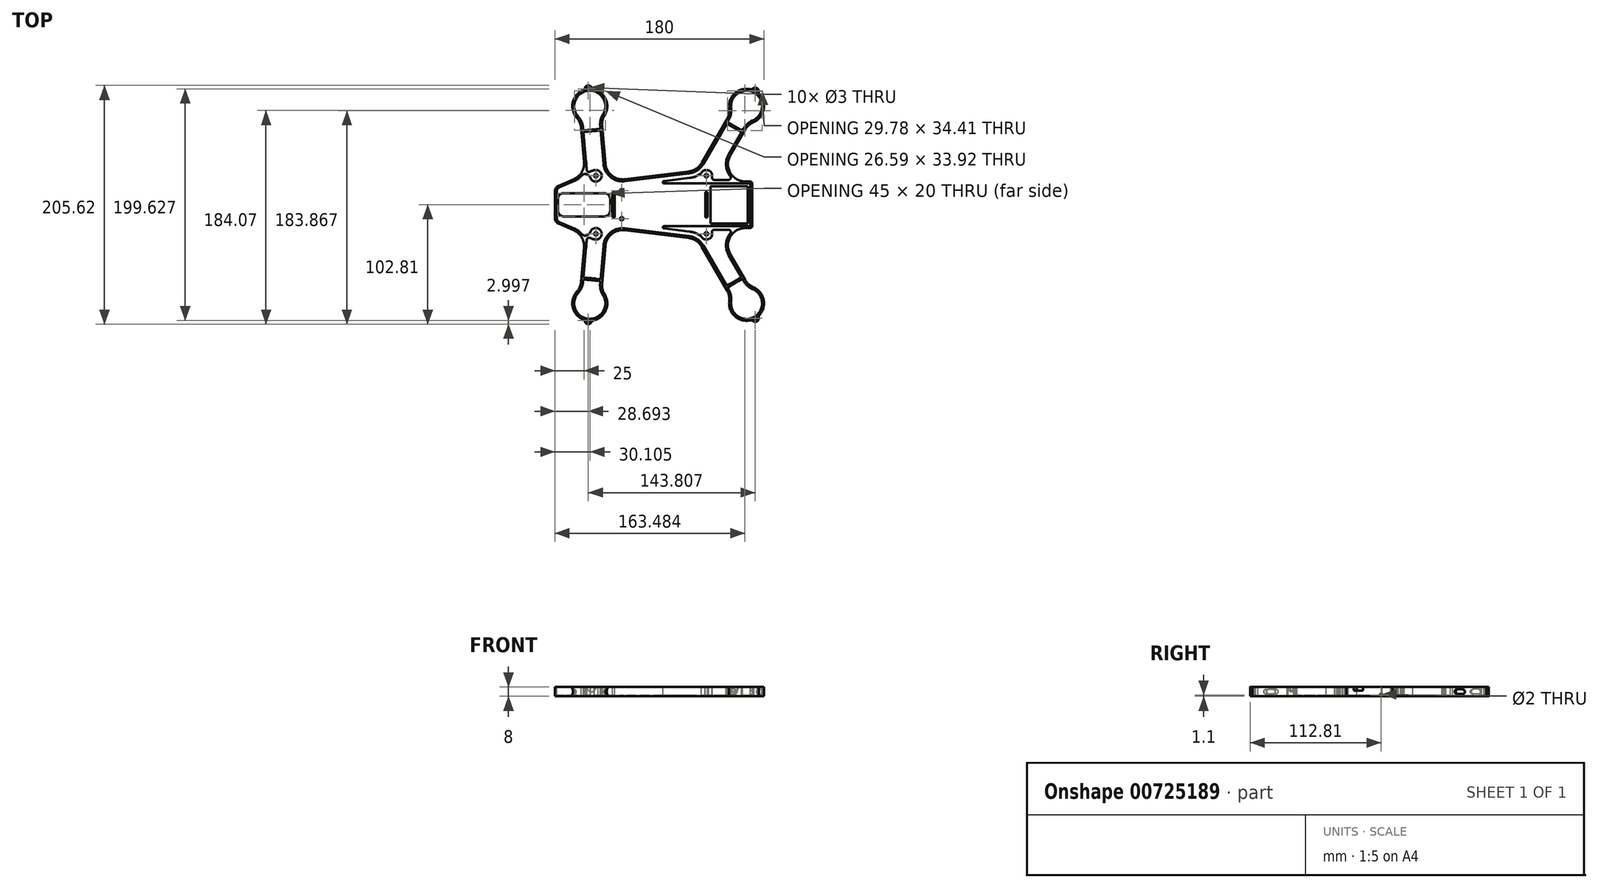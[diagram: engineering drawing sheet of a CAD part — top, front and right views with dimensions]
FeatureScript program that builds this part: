
annotation { "Feature Type Name" : "Feature", "Feature Type Description" : "" }
export const myFeature = defineFeature(function(context is Context, id is Id, definition is map)
    precondition{}
    {
        {
            var Q0;
            Q0=qCreatedBy(makeId("Top.planeOp"),FACE);
            var sketch = newSketch(context, id + "F0", { "sketchPlane" : qUnion([Q0])});
            skLineSegment(sketch, "E0", {"start": v(-85, 0) * mm, "end": v(85, 0) * mm, "construction": true});
            skLineSegment(sketch, "E1", {"start": v(-47.57, 0) * mm, "end": v(-55, -84.87) * mm, "construction": true});
            skLineSegment(sketch, "E2", {"start": v(31, 0) * mm, "end": v(80, -84.87) * mm, "construction": true});
            skArc(sketch, "E3", {"start": v(-66.17, -74.86) * mm, "mid": v(-69.65, -88.1) * mm, "end": v(-60.9, -98.66) * mm});
            skArc(sketch, "E4", {"start": v(65.1, -83.08) * mm, "mid": v(69.86, -95.92) * mm, "end": v(83.07, -99.55) * mm});
            skLineSegment(sketch, "E5", {"start": v(-85, 0) * mm, "end": v(-85, -11.72) * mm});
            skLineSegment(sketch, "E6", {"start": v(-59.85, -37.08) * mm, "end": v(-62.4, -66.15) * mm});
            skLineSegment(sketch, "E7", {"start": v(-44.47, -67.72) * mm, "end": v(-41.64, -35.47) * mm});
            skLineSegment(sketch, "E8", {"start": v(-24.87, -21.9) * mm, "end": v(30.26, -28.66) * mm});
            skLineSegment(sketch, "E9", {"start": v(41.42, -36.05) * mm, "end": v(63.2, -73.78) * mm});
            skLineSegment(sketch, "E10", {"start": v(78.8, -64.78) * mm, "end": v(65.93, -42.5) * mm});
            skLineSegment(sketch, "E11", {"start": v(78.92, -20) * mm, "end": v(83, -20) * mm});
            skLineSegment(sketch, "E12", {"start": v(85, -18) * mm, "end": v(85, 0) * mm});
            skPoint(sketch, "E13.visualSharp", {"position": v(-40.3, -20) * mm});
            skArc(sketch, "E13.filletArc", {"start": v(-24.87, -21.9) * mm, "mid": v(-36.14, -25.12) * mm, "end": v(-41.64, -35.47) * mm});
            skPoint(sketch, "E14.visualSharp", {"position": v(52.94, -20) * mm});
            skPoint(sketch, "E15.visualSharp", {"position": v(37.68, -29.57) * mm});
            skArc(sketch, "E15.filletArc", {"start": v(41.42, -36.05) * mm, "mid": v(36.71, -31.04) * mm, "end": v(30.26, -28.66) * mm});
            skPoint(sketch, "E16.visualSharp", {"position": v(85, -20) * mm});
            skArc(sketch, "E16.filletArc", {"start": v(83, -20) * mm, "mid": v(84.41, -19.41) * mm, "end": v(85, -18) * mm});
            skArc(sketch, "E17.filletArc", {"start": v(78.92, -20) * mm, "mid": v(65.93, -27.5) * mm, "end": v(65.93, -42.5) * mm});
            skPoint(sketch, "E18.visualSharp", {"position": v(-62.92, -72.13) * mm});
            skArc(sketch, "E18.filletArc", {"start": v(-66.17, -74.86) * mm, "mid": v(-63.58, -70.81) * mm, "end": v(-62.4, -66.15) * mm});
            skPoint(sketch, "E19.visualSharp", {"position": v(-44.99, -73.7) * mm});
            skArc(sketch, "E19.filletArc", {"start": v(-44.47, -67.72) * mm, "mid": v(-44.11, -72.52) * mm, "end": v(-42.26, -76.95) * mm});
            skArc(sketch, "E20.filletArc", {"start": v(65.1, -83.08) * mm, "mid": v(64.91, -78.27) * mm, "end": v(63.2, -73.78) * mm});
            skPoint(sketch, "E21.visualSharp", {"position": v(81.8, -69.98) * mm});
            skArc(sketch, "E21.filletArc", {"start": v(78.8, -64.78) * mm, "mid": v(81.83, -68.5) * mm, "end": v(85.9, -71.08) * mm});
            skLineSegment(sketch, "E22", {"start": v(-81.99, -16.3) * mm, "end": v(-68.83, -22) * mm});
            skPoint(sketch, "E23.visualSharp", {"position": v(-85, -15) * mm});
            skArc(sketch, "E23.filletArc", {"start": v(-85, -11.72) * mm, "mid": v(-84.18, -14.46) * mm, "end": v(-81.99, -16.3) * mm});
            skPoint(sketch, "E24.visualSharp", {"position": v(-58.91, -26.3) * mm});
            skArc(sketch, "E25.filletArc", {"start": v(-59.85, -37.08) * mm, "mid": v(-61.9, -28.1) * mm, "end": v(-68.83, -22) * mm});
            skLineSegment(sketch, "E26", {"start": v(78.92, -20) * mm, "end": v(-122.08, -20) * mm, "construction": true});
            skLineSegment(sketch, "E27", {"start": v(-55, -84.87) * mm, "end": v(-57.29, -111.02) * mm, "construction": true});
            skLineSegment(sketch, "E28", {"start": v(80, -84.87) * mm, "end": v(94.45, -109.9) * mm, "construction": true});
            skArc(sketch, "E29.trimOffspring", {"start": v(-51.58, -99.47) * mm, "mid": v(-41.14, -90.6) * mm, "end": v(-42.26, -76.95) * mm});
            skCircle(sketch, "E30", {"center": v(87.5, -97.86) * mm, "radius": 1.5 * mm});
            skArc(sketch, "E31", {"start": v(85.6, -100.18) * mm, "mid": v(89, -100.46) * mm, "end": v(90.46, -97.37) * mm});
            skArc(sketch, "E32.trimOffspring", {"start": v(91.18, -94.87) * mm, "mid": v(94.64, -81.62) * mm, "end": v(85.9, -71.08) * mm});
            skPoint(sketch, "E33.visualSharp", {"position": v(89.94, -96.1) * mm});
            skArc(sketch, "E33.filletArc", {"start": v(91.18, -94.87) * mm, "mid": v(90.54, -96.04) * mm, "end": v(90.46, -97.37) * mm});
            skPoint(sketch, "E34.visualSharp", {"position": v(84.76, -99.1) * mm});
            skArc(sketch, "E35.filletArc", {"start": v(85.6, -100.18) * mm, "mid": v(84.4, -99.58) * mm, "end": v(83.07, -99.55) * mm});
            skCircle(sketch, "E36", {"center": v(-49.76, -25) * mm, "radius": 1.5 * mm});
            skCircle(sketch, "E37", {"center": v(45.43, -25) * mm, "radius": 1.5 * mm});
            skCircle(sketch, "E38", {"center": v(-56.3, -99.81) * mm, "radius": 1.5 * mm});
            skArc(sketch, "E39", {"start": v(-59.2, -100.61) * mm, "mid": v(-56.57, -102.8) * mm, "end": v(-53.6, -101.1) * mm});
            skPoint(sketch, "E40.visualSharp", {"position": v(-53.3, -99.77) * mm});
            skArc(sketch, "E40.filletArc", {"start": v(-51.58, -99.47) * mm, "mid": v(-52.77, -100.06) * mm, "end": v(-53.6, -101.1) * mm});
            skPoint(sketch, "E41.visualSharp", {"position": v(-59.25, -99.25) * mm});
            skArc(sketch, "E41.filletArc", {"start": v(-59.2, -100.61) * mm, "mid": v(-59.83, -99.44) * mm, "end": v(-60.9, -98.66) * mm});
            skLineSegment(sketch, "E42", {"start": v(-55, -84.87) * mm, "end": v(80, -84.87) * mm, "construction": true});
            skLineSegment(sketch, "E43", {"start": v(85, -15) * mm, "end": v(-122.38, -15) * mm, "construction": true});
            skLineSegment(sketch, "E44.2", {"start": v(78.92, -18.4) * mm, "end": v(80, -18.4) * mm});
            skLineSegment(sketch, "E44.4", {"start": v(77.4, -65.58) * mm, "end": v(76.4, -63.85) * mm});
            skArc(sketch, "E44.5", {"start": v(-51.94, -97.92) * mm, "mid": v(-42.62, -90) * mm, "end": v(-43.62, -77.8) * mm});
            skArc(sketch, "E44.8", {"start": v(-64.98, -75.93) * mm, "mid": v(-66.53, -91.7) * mm, "end": v(-51.94, -97.92) * mm});
            skArc(sketch, "E44.9", {"start": v(-64.98, -75.93) * mm, "mid": v(-62.1, -71.45) * mm, "end": v(-60.8, -66.3) * mm});
            skArc(sketch, "E44.15", {"start": v(-46.06, -67.58) * mm, "mid": v(-45.67, -72.89) * mm, "end": v(-43.62, -77.8) * mm});
            skLineSegment(sketch, "E44.16", {"start": v(-46.06, -67.58) * mm, "end": v(-45.89, -65.6) * mm});
            skLineSegment(sketch, "E44.19", {"start": v(30.45, -27.07) * mm, "end": v(30.45, -27.07) * mm});
            skArc(sketch, "E44.21", {"start": v(66.7, -83.27) * mm, "mid": v(66.48, -77.95) * mm, "end": v(64.6, -72.98) * mm});
            skArc(sketch, "E44.22", {"start": v(66.7, -83.27) * mm, "mid": v(74.48, -97.08) * mm, "end": v(89.99, -93.8) * mm});
            skArc(sketch, "E44.25", {"start": v(89.99, -93.8) * mm, "mid": v(93.08, -81.96) * mm, "end": v(85.26, -72.55) * mm});
            skArc(sketch, "E44.26", {"start": v(77.4, -65.58) * mm, "mid": v(80.77, -69.7) * mm, "end": v(85.26, -72.55) * mm});
            skPoint(sketch, "E45.visualSharp", {"position": v(-2, -22.69) * mm});
            skPoint(sketch, "E46.visualSharp", {"position": v(2, -23.18) * mm});
            skLineSegment(sketch, "E47.trimOffspring", {"start": v(-43.24, -35.33) * mm, "end": v(-43.24, -35.33) * mm});
            skLineSegment(sketch, "E48.MirrorCS", {"start": v(78.92, 20) * mm, "end": v(83, 20) * mm});
            skArc(sketch, "E49.MirrorCS", {"start": v(91.18, 94.87) * mm, "mid": v(90.54, 96.04) * mm, "end": v(90.46, 97.37) * mm});
            skLineSegment(sketch, "E50.MirrorCS", {"start": v(78.92, 18.4) * mm, "end": v(80, 18.4) * mm});
            skArc(sketch, "E51.MirrorCS", {"start": v(85.6, 100.18) * mm, "mid": v(84.4, 99.58) * mm, "end": v(83.07, 99.55) * mm});
            skPoint(sketch, "E52.MirrorP", {"position": v(-58.91, 26.3) * mm});
            skPoint(sketch, "E53.MirrorP", {"position": v(52.94, 20) * mm});
            skCircle(sketch, "E54.MirrorC", {"center": v(-56.3, 99.81) * mm, "radius": 1.5 * mm});
            skPoint(sketch, "E55.MirrorP", {"position": v(84.76, 99.1) * mm});
            skArc(sketch, "E56.MirrorCS", {"start": v(-64.98, 75.93) * mm, "mid": v(-62.1, 71.45) * mm, "end": v(-60.8, 66.3) * mm});
            skLineSegment(sketch, "E57.MirrorCS", {"start": v(-44.47, 67.72) * mm, "end": v(-41.64, 35.47) * mm});
            skLineSegment(sketch, "E58.MirrorCS", {"start": v(80, 84.87) * mm, "end": v(94.45, 109.9) * mm, "construction": true});
            skPoint(sketch, "E59.MirrorP", {"position": v(-62.92, 72.13) * mm});
            skPoint(sketch, "E60.MirrorP", {"position": v(-59.25, 99.25) * mm});
            skArc(sketch, "E61.MirrorCS", {"start": v(-24.87, 21.9) * mm, "mid": v(-36.14, 25.12) * mm, "end": v(-41.64, 35.47) * mm});
            skArc(sketch, "E62.MirrorCS", {"start": v(-85, 11.72) * mm, "mid": v(-84.18, 14.46) * mm, "end": v(-81.99, 16.3) * mm});
            skPoint(sketch, "E63.MirrorP", {"position": v(37.68, 29.57) * mm});
            skArc(sketch, "E64.MirrorCS", {"start": v(89.99, 93.8) * mm, "mid": v(93.08, 81.96) * mm, "end": v(85.26, 72.55) * mm});
            skLineSegment(sketch, "E65.MirrorCS", {"start": v(77.4, 65.58) * mm, "end": v(76.4, 63.85) * mm});
            skLineSegment(sketch, "E66.MirrorCS", {"start": v(-24.87, 21.9) * mm, "end": v(30.26, 28.66) * mm});
            skPoint(sketch, "E67.MirrorP", {"position": v(89.94, 96.1) * mm});
            skLineSegment(sketch, "E68.MirrorCS", {"start": v(30.45, 27.07) * mm, "end": v(30.45, 27.07) * mm});
            skCircle(sketch, "E69.MirrorC", {"center": v(45.43, 25) * mm, "radius": 1.5 * mm});
            skCircle(sketch, "E70.MirrorC", {"center": v(87.5, 97.86) * mm, "radius": 1.5 * mm});
            skLineSegment(sketch, "E71.MirrorCS", {"start": v(-55, 84.87) * mm, "end": v(80, 84.87) * mm, "construction": true});
            skArc(sketch, "E72.MirrorCS", {"start": v(-59.2, 100.61) * mm, "mid": v(-56.57, 102.8) * mm, "end": v(-53.6, 101.1) * mm});
            skLineSegment(sketch, "E73.MirrorCS", {"start": v(31, 0) * mm, "end": v(80, 84.87) * mm, "construction": true});
            skArc(sketch, "E74.MirrorCS", {"start": v(-66.17, 74.86) * mm, "mid": v(-63.58, 70.81) * mm, "end": v(-62.4, 66.15) * mm});
            skLineSegment(sketch, "E75.MirrorCS", {"start": v(85, 15) * mm, "end": v(-122.38, 15) * mm, "construction": true});
            skLineSegment(sketch, "E76.MirrorCS", {"start": v(-43.24, 35.33) * mm, "end": v(-43.24, 35.33) * mm});
            skArc(sketch, "E77.MirrorCS", {"start": v(77.4, 65.58) * mm, "mid": v(80.77, 69.7) * mm, "end": v(85.26, 72.55) * mm});
            skPoint(sketch, "E78.MirrorP", {"position": v(-2, 22.69) * mm});
            skArc(sketch, "E79.MirrorCS", {"start": v(-66.17, 74.86) * mm, "mid": v(-69.65, 88.1) * mm, "end": v(-60.9, 98.66) * mm});
            skPoint(sketch, "E80.MirrorP", {"position": v(81.8, 69.98) * mm});
            skLineSegment(sketch, "E81.MirrorCS", {"start": v(-46.06, 67.58) * mm, "end": v(-45.89, 65.6) * mm});
            skArc(sketch, "E82.MirrorCS", {"start": v(78.8, 64.78) * mm, "mid": v(81.83, 68.5) * mm, "end": v(85.9, 71.08) * mm});
            skArc(sketch, "E83.MirrorCS", {"start": v(-59.85, 37.08) * mm, "mid": v(-61.9, 28.1) * mm, "end": v(-68.83, 22) * mm});
            skLineSegment(sketch, "E84.MirrorCS", {"start": v(78.92, 20) * mm, "end": v(-122.08, 20) * mm, "construction": true});
            skArc(sketch, "E85.MirrorCS", {"start": v(66.7, 83.27) * mm, "mid": v(74.48, 97.08) * mm, "end": v(89.99, 93.8) * mm});
            skArc(sketch, "E86.MirrorCS", {"start": v(65.1, 83.08) * mm, "mid": v(69.86, 95.92) * mm, "end": v(83.07, 99.55) * mm});
            skArc(sketch, "E87.MirrorCS", {"start": v(-51.58, 99.47) * mm, "mid": v(-41.14, 90.6) * mm, "end": v(-42.26, 76.95) * mm});
            skPoint(sketch, "E88.MirrorP", {"position": v(-53.3, 99.77) * mm});
            skArc(sketch, "E89.MirrorCS", {"start": v(91.18, 94.87) * mm, "mid": v(94.64, 81.62) * mm, "end": v(85.9, 71.08) * mm});
            skArc(sketch, "E90.MirrorCS", {"start": v(41.42, 36.05) * mm, "mid": v(36.71, 31.04) * mm, "end": v(30.26, 28.66) * mm});
            skArc(sketch, "E91.MirrorCS", {"start": v(-64.98, 75.93) * mm, "mid": v(-66.53, 91.7) * mm, "end": v(-51.94, 97.92) * mm});
            skArc(sketch, "E92.MirrorCS", {"start": v(-51.94, 97.92) * mm, "mid": v(-42.62, 90) * mm, "end": v(-43.62, 77.8) * mm});
            skArc(sketch, "E93.MirrorCS", {"start": v(-44.47, 67.72) * mm, "mid": v(-44.11, 72.52) * mm, "end": v(-42.26, 76.95) * mm});
            skLineSegment(sketch, "E94.MirrorCS", {"start": v(-47.57, 0) * mm, "end": v(-55, 84.87) * mm, "construction": true});
            skLineSegment(sketch, "E95.MirrorCS", {"start": v(78.8, 64.78) * mm, "end": v(65.93, 42.5) * mm});
            skLineSegment(sketch, "E96.MirrorCS", {"start": v(41.42, 36.05) * mm, "end": v(63.2, 73.78) * mm});
            skArc(sketch, "E97.MirrorCS", {"start": v(85.6, 100.18) * mm, "mid": v(89, 100.46) * mm, "end": v(90.46, 97.37) * mm});
            skArc(sketch, "E98.MirrorCS", {"start": v(-46.06, 67.58) * mm, "mid": v(-45.67, 72.89) * mm, "end": v(-43.62, 77.8) * mm});
            skLineSegment(sketch, "E99.MirrorCS", {"start": v(-85, 0) * mm, "end": v(-85, 11.72) * mm});
            skArc(sketch, "E100.MirrorCS", {"start": v(65.1, 83.08) * mm, "mid": v(64.91, 78.27) * mm, "end": v(63.2, 73.78) * mm});
            skArc(sketch, "E101.MirrorCS", {"start": v(78.92, 20) * mm, "mid": v(65.93, 27.5) * mm, "end": v(65.93, 42.5) * mm});
            skArc(sketch, "E102.MirrorCS", {"start": v(66.7, 83.27) * mm, "mid": v(66.48, 77.95) * mm, "end": v(64.6, 72.98) * mm});
            skLineSegment(sketch, "E103.MirrorCS", {"start": v(-55, 84.87) * mm, "end": v(-57.29, 111.02) * mm, "construction": true});
            skPoint(sketch, "E104.MirrorP", {"position": v(-44.99, 73.7) * mm});
            skCircle(sketch, "E105.MirrorC", {"center": v(-49.76, 25) * mm, "radius": 1.5 * mm});
            skPoint(sketch, "E106.MirrorP", {"position": v(-85, 15) * mm});
            skPoint(sketch, "E107.MirrorP", {"position": v(85, 20) * mm});
            skLineSegment(sketch, "E108.MirrorCS", {"start": v(85, 18) * mm, "end": v(85, 0) * mm});
            skArc(sketch, "E109.MirrorCS", {"start": v(83, 20) * mm, "mid": v(84.41, 19.41) * mm, "end": v(85, 18) * mm});
            skPoint(sketch, "E110.MirrorP", {"position": v(-40.3, 20) * mm});
            skLineSegment(sketch, "E111.MirrorCS", {"start": v(-81.99, 16.3) * mm, "end": v(-68.83, 22) * mm});
            skLineSegment(sketch, "E112.MirrorCS", {"start": v(-59.85, 37.08) * mm, "end": v(-62.4, 66.15) * mm});
            skPoint(sketch, "E113.MirrorP", {"position": v(2, 23.18) * mm});
            skArc(sketch, "E114.filletArc", {"start": v(-60.9, 98.66) * mm, "mid": v(-59.83, 99.44) * mm, "end": v(-59.2, 100.61) * mm});
            skArc(sketch, "E115.filletArc", {"start": v(-53.6, 101.1) * mm, "mid": v(-52.77, 100.06) * mm, "end": v(-51.58, 99.47) * mm});
            skLineSegment(sketch, "E116", {"start": v(-60.63, -64.3) * mm, "end": v(-45.89, -65.6) * mm});
            skLineSegment(sketch, "E117.trimOffspring", {"start": v(-60.63, -64.3) * mm, "end": v(-60.8, -66.3) * mm});
            skLineSegment(sketch, "E118", {"start": v(63.6, -71.25) * mm, "end": v(76.4, -63.85) * mm});
            skLineSegment(sketch, "E119.trimOffspring", {"start": v(63.6, -71.25) * mm, "end": v(64.6, -72.98) * mm});
            skLineSegment(sketch, "E120.MirrorCS", {"start": v(-60.63, 64.3) * mm, "end": v(-45.89, 65.6) * mm});
            skLineSegment(sketch, "E121.MirrorCS", {"start": v(63.6, 71.25) * mm, "end": v(76.4, 63.85) * mm});
            skLineSegment(sketch, "E122.trimOffspring", {"start": v(63.6, 71.25) * mm, "end": v(64.6, 72.98) * mm});
            skLineSegment(sketch, "E123.trimOffspring", {"start": v(-60.63, 64.3) * mm, "end": v(-60.8, 66.3) * mm});
            skCircle(sketch, "E124", {"center": v(0, 0) * mm, "radius": 134.27 * mm, "construction": true});
            skLineSegment(sketch, "E125.bottom", {"start": v(-42.5, -10) * mm, "end": v(-77.5, -10) * mm});
            skLineSegment(sketch, "E125.top", {"start": v(-42.5, 10) * mm, "end": v(-77.5, 10) * mm});
            skLineSegment(sketch, "E125.left", {"start": v(-37.5, -5) * mm, "end": v(-37.5, 5) * mm});
            skLineSegment(sketch, "E125.right", {"start": v(-82.5, -5) * mm, "end": v(-82.5, 5) * mm});
            skArc(sketch, "E126.filletArc", {"start": v(-37.5, 5) * mm, "mid": v(-38.96, 8.54) * mm, "end": v(-42.5, 10) * mm});
            skArc(sketch, "E127.filletArc", {"start": v(-82.5, -5) * mm, "mid": v(-81.04, -8.54) * mm, "end": v(-77.5, -10) * mm});
            skArc(sketch, "E128.filletArc", {"start": v(-77.5, 10) * mm, "mid": v(-81.04, 8.54) * mm, "end": v(-82.5, 5) * mm});
            skArc(sketch, "E129.filletArc", {"start": v(-42.5, -10) * mm, "mid": v(-38.96, -8.54) * mm, "end": v(-37.5, -5) * mm});
            skCircle(sketch, "E130", {"center": v(-27.5, -12) * mm, "radius": 1.5 * mm});
            skCircle(sketch, "E131.MirrorC", {"center": v(-27.5, 12) * mm, "radius": 1.5 * mm});
            skSolve(sketch);
        }
        {
            var Q0;
            Q0=makeQuery(id+"F0.imprint","IMPRINT",FACE,{"disambiguationData":[TD([[makeQuery(id+"F0.imprint","IMPRINT",EDGE,{"derivedFrom":sQuery(id+"F0.wireOp",EDGE,"E3")}),1.0]])]});
            extrude(context, id + "F1", {"entities" : qUnion([Q0]), "depth" : 8 * mm});
        }
        {
            var Q0;
            Q0=makeQuery(id+"F1.opExtrude","CAP_FACE",FACE,{"disambiguationData":[OSD([sQuery(id+"F0.wireOp",EDGE,"E3"),sQuery(id+"F0.wireOp",EDGE,"E4"),sQuery(id+"F0.wireOp",EDGE,"E5"),sQuery(id+"F0.wireOp",EDGE,"E6"),sQuery(id+"F0.wireOp",EDGE,"E7"),sQuery(id+"F0.wireOp",EDGE,"E8"),sQuery(id+"F0.wireOp",EDGE,"E9"),sQuery(id+"F0.wireOp",EDGE,"E10"),sQuery(id+"F0.wireOp",EDGE,"E11"),sQuery(id+"F0.wireOp",EDGE,"E12"),sQuery(id+"F0.wireOp",EDGE,"E13.filletArc"),sQuery(id+"F0.wireOp",EDGE,"E15.filletArc"),sQuery(id+"F0.wireOp",EDGE,"E16.filletArc"),sQuery(id+"F0.wireOp",EDGE,"E17.filletArc"),sQuery(id+"F0.wireOp",EDGE,"E18.filletArc"),sQuery(id+"F0.wireOp",EDGE,"E19.filletArc"),sQuery(id+"F0.wireOp",EDGE,"E20.filletArc"),sQuery(id+"F0.wireOp",EDGE,"E21.filletArc"),sQuery(id+"F0.wireOp",EDGE,"E22"),sQuery(id+"F0.wireOp",EDGE,"E23.filletArc"),sQuery(id+"F0.wireOp",EDGE,"E25.filletArc"),sQuery(id+"F0.wireOp",EDGE,"E29.trimOffspring"),sQuery(id+"F0.wireOp",EDGE,"E30"),sQuery(id+"F0.wireOp",EDGE,"E31"),sQuery(id+"F0.wireOp",EDGE,"E32.trimOffspring"),sQuery(id+"F0.wireOp",EDGE,"E33.filletArc"),sQuery(id+"F0.wireOp",EDGE,"E35.filletArc"),sQuery(id+"F0.wireOp",EDGE,"E36"),sQuery(id+"F0.wireOp",EDGE,"E37"),sQuery(id+"F0.wireOp",EDGE,"E38"),sQuery(id+"F0.wireOp",EDGE,"E39"),sQuery(id+"F0.wireOp",EDGE,"E40.filletArc"),sQuery(id+"F0.wireOp",EDGE,"E41.filletArc"),sQuery(id+"F0.wireOp",EDGE,"E44.4"),sQuery(id+"F0.wireOp",EDGE,"E44.5"),sQuery(id+"F0.wireOp",EDGE,"E44.8"),sQuery(id+"F0.wireOp",EDGE,"E44.9"),sQuery(id+"F0.wireOp",EDGE,"E44.10"),sQuery(id+"F0.wireOp",EDGE,"E44.11"),sQuery(id+"F0.wireOp",EDGE,"E44.12"),sQuery(id+"F0.wireOp",EDGE,"E44.13"),sQuery(id+"F0.wireOp",EDGE,"E44.15"),sQuery(id+"F0.wireOp",EDGE,"E44.16"),sQuery(id+"F0.wireOp",EDGE,"E44.20"),sQuery(id+"F0.wireOp",EDGE,"E44.21"),sQuery(id+"F0.wireOp",EDGE,"E44.22"),sQuery(id+"F0.wireOp",EDGE,"E44.25"),sQuery(id+"F0.wireOp",EDGE,"E44.26"),sQuery(id+"F0.wireOp",EDGE,"55a75c94-3981-4925-938c-0703a2540f2a"),sQuery(id+"F0.wireOp",EDGE,"18e9a88f-63d2-484e-94f8-6aafb132c643"),sQuery(id+"F0.wireOp",EDGE,"3e357946-6a65-48ba-9413-4c9084a4b4eb"),sQuery(id+"F0.wireOp",EDGE,"9b53bd53-ce0e-4c03-85f3-8b744b70c49f.trimOffspring"),sQuery(id+"F0.wireOp",EDGE,"E48.MirrorCS"),sQuery(id+"F0.wireOp",EDGE,"E49.MirrorCS"),sQuery(id+"F0.wireOp",EDGE,"E51.MirrorCS"),sQuery(id+"F0.wireOp",EDGE,"E54.MirrorC"),sQuery(id+"F0.wireOp",EDGE,"E56.MirrorCS"),sQuery(id+"F0.wireOp",EDGE,"E57.MirrorCS"),sQuery(id+"F0.wireOp",EDGE,"E61.MirrorCS"),sQuery(id+"F0.wireOp",EDGE,"E62.MirrorCS"),sQuery(id+"F0.wireOp",EDGE,"E64.MirrorCS"),sQuery(id+"F0.wireOp",EDGE,"E65.MirrorCS"),sQuery(id+"F0.wireOp",EDGE,"E66.MirrorCS"),sQuery(id+"F0.wireOp",EDGE,"E69.MirrorC"),sQuery(id+"F0.wireOp",EDGE,"E508.MirrorCS"),sQuery(id+"F0.wireOp",EDGE,"E70.MirrorC"),sQuery(id+"F0.wireOp",EDGE,"7aa77c07-5236-4930-a80c-88c67a00b59931.MirrorCS"),sQuery(id+"F0.wireOp",EDGE,"E72.MirrorCS"),sQuery(id+"F0.wireOp",EDGE,"E74.MirrorCS"),sQuery(id+"F0.wireOp",EDGE,"7aa77c07-5236-4930-a80c-88c67a00b59935.MirrorCS"),sQuery(id+"F0.wireOp",EDGE,"7aa77c07-5236-4930-a80c-88c67a00b59937.MirrorCS"),sQuery(id+"F0.wireOp",EDGE,"E77.MirrorCS"),sQuery(id+"F0.wireOp",EDGE,"E79.MirrorCS"),sQuery(id+"F0.wireOp",EDGE,"E81.MirrorCS"),sQuery(id+"F0.wireOp",EDGE,"E82.MirrorCS"),sQuery(id+"F0.wireOp",EDGE,"E83.MirrorCS"),sQuery(id+"F0.wireOp",EDGE,"E85.MirrorCS"),sQuery(id+"F0.wireOp",EDGE,"E86.MirrorCS"),sQuery(id+"F0.wireOp",EDGE,"E87.MirrorCS"),sQuery(id+"F0.wireOp",EDGE,"E89.MirrorCS"),sQuery(id+"F0.wireOp",EDGE,"E90.MirrorCS"),sQuery(id+"F0.wireOp",EDGE,"E91.MirrorCS"),sQuery(id+"F0.wireOp",EDGE,"E92.MirrorCS"),sQuery(id+"F0.wireOp",EDGE,"E93.MirrorCS"),sQuery(id+"F0.wireOp",EDGE,"E95.MirrorCS"),sQuery(id+"F0.wireOp",EDGE,"E96.MirrorCS"),sQuery(id+"F0.wireOp",EDGE,"E97.MirrorCS"),sQuery(id+"F0.wireOp",EDGE,"E98.MirrorCS"),sQuery(id+"F0.wireOp",EDGE,"E99.MirrorCS"),sQuery(id+"F0.wireOp",EDGE,"E100.MirrorCS"),sQuery(id+"F0.wireOp",EDGE,"E101.MirrorCS"),sQuery(id+"F0.wireOp",EDGE,"E102.MirrorCS"),sQuery(id+"F0.wireOp",EDGE,"7aa77c07-5236-4930-a80c-88c67a00b59970.MirrorCS"),sQuery(id+"F0.wireOp",EDGE,"E105.MirrorC"),sQuery(id+"F0.wireOp",EDGE,"7aa77c07-5236-4930-a80c-88c67a00b59978.MirrorCS"),sQuery(id+"F0.wireOp",EDGE,"7aa77c07-5236-4930-a80c-88c67a00b59979.MirrorCS"),sQuery(id+"F0.wireOp",EDGE,"E530.MirrorCS"),sQuery(id+"F0.wireOp",EDGE,"E108.MirrorCS"),sQuery(id+"F0.wireOp",EDGE,"E109.MirrorCS"),sQuery(id+"F0.wireOp",EDGE,"E111.MirrorCS"),sQuery(id+"F0.wireOp",EDGE,"E112.MirrorCS"),sQuery(id+"F0.wireOp",EDGE,"E537.MirrorCS"),sQuery(id+"F0.wireOp",EDGE,"E114.filletArc"),sQuery(id+"F0.wireOp",EDGE,"E115.filletArc"),sQuery(id+"F0.wireOp",EDGE,"a4d90b42-d63e-410f-917a-941b09824992"),sQuery(id+"F0.wireOp",EDGE,"E116"),sQuery(id+"F0.wireOp",EDGE,"cMJuFud1-vg0K-iN1q-p5d7-nlo64yB5XbXq"),sQuery(id+"F0.wireOp",EDGE,"E117.trimOffspring"),sQuery(id+"F0.wireOp",EDGE,"74f08385-9b30-422e-95e3-7c0d5ab4f87f.trimOffspring"),sQuery(id+"F0.wireOp",EDGE,"E118"),sQuery(id+"F0.wireOp",EDGE,"s3oDME9j-RjMK-g1Hw-ZGjj-mhpWrOwCSelL"),sQuery(id+"F0.wireOp",EDGE,"b3e49e08-c0df-423a-bc82-550474e4bf9f.trimOffspring"),sQuery(id+"F0.wireOp",EDGE,"E119.trimOffspring"),sQuery(id+"F0.wireOp",EDGE,"31413146-a01f-4e31-a23e-b78ac6f1261a0.MirrorCS"),sQuery(id+"F0.wireOp",EDGE,"E120.MirrorCS"),sQuery(id+"F0.wireOp",EDGE,"14c246ef-2517-462f-98e1-722c737d70360.MirrorCS"),sQuery(id+"F0.wireOp",EDGE,"E121.MirrorCS"),sQuery(id+"F0.wireOp",EDGE,"35ee15a8-cd36-4e2e-a5d4-a9be4718c77d.trimOffspring"),sQuery(id+"F0.wireOp",EDGE,"E122.trimOffspring"),sQuery(id+"F0.wireOp",EDGE,"3fd240ab-1996-4fb1-8bde-4f594ce2e648.trimOffspring"),sQuery(id+"F0.wireOp",EDGE,"E123.trimOffspring")])],"isStart":false});
            var sketch = newSketch(context, id + "F2", { "sketchPlane" : qUnion([Q0])});
            skLineSegment(sketch, "E132.MirrorCS", {"start": v(78.92, 18.4) * mm, "end": v(78.92, 18.4) * mm});
            skLineSegment(sketch, "E133", {"start": v(78.92, -18.4) * mm, "end": v(8.98, -18.4) * mm});
            skLineSegment(sketch, "E134", {"start": v(78.92, -18.4) * mm, "end": v(-100.25, -18.4) * mm, "construction": true});
            skPoint(sketch, "E135", {"position": v(45.4, -10) * mm});
            skPoint(sketch, "E136", {"position": v(45.4, 10) * mm});
            skLineSegment(sketch, "E137", {"start": v(45.4, 10) * mm, "end": v(45.4, -10) * mm, "construction": true});
            skArc(sketch, "E138.0.startCap", {"start": v(44.4, 10) * mm, "mid": v(45.4, 11) * mm, "end": v(46.4, 10) * mm});
            skArc(sketch, "E138.0.endCap", {"start": v(46.4, -10) * mm, "mid": v(45.4, -11) * mm, "end": v(44.4, -10) * mm});
            skLineSegment(sketch, "E138.0.left", {"start": v(46.4, 10) * mm, "end": v(46.4, -10) * mm});
            skLineSegment(sketch, "E138.0.right", {"start": v(44.4, 10) * mm, "end": v(44.4, -10) * mm});
            skLineSegment(sketch, "E139.2.0.0", {"start": v(-35.4, 10) * mm, "end": v(-35.4, -10) * mm});
            skLineSegment(sketch, "E139.2.0.1", {"start": v(-33.4, 10) * mm, "end": v(-33.4, -10) * mm});
            skArc(sketch, "E139.2.0.2", {"start": v(-35.4, 10) * mm, "mid": v(-34.4, 11) * mm, "end": v(-33.4, 10) * mm});
            skArc(sketch, "E139.2.0.3", {"start": v(-33.4, -10) * mm, "mid": v(-34.4, -11) * mm, "end": v(-35.4, -10) * mm});
            skLineSegment(sketch, "E140.0", {"start": v(83, 18.4) * mm, "end": v(78.92, 18.4) * mm});
            skArc(sketch, "E140.1", {"start": v(83.4, 18) * mm, "mid": v(83.28, 18.28) * mm, "end": v(83, 18.4) * mm});
            skLineSegment(sketch, "E140.2", {"start": v(83.4, -18) * mm, "end": v(83.4, 18) * mm});
            skArc(sketch, "E140.3", {"start": v(83, -18.4) * mm, "mid": v(83.28, -18.28) * mm, "end": v(83.4, -18) * mm});
            skLineSegment(sketch, "E140.4", {"start": v(78.92, -18.4) * mm, "end": v(83, -18.4) * mm});
            skArc(sketch, "E140.5", {"start": v(64.54, -43.3) * mm, "mid": v(62.37, -33.76) * mm, "end": v(65.94, -24.65) * mm});
            skLineSegment(sketch, "E140.6", {"start": v(75.6, -62.46) * mm, "end": v(64.54, -43.3) * mm});
            skLineSegment(sketch, "E140.10", {"start": v(-60.49, 62.7) * mm, "end": v(-58.26, 37.22) * mm});
            skLineSegment(sketch, "E140.18", {"start": v(-43.24, 35.33) * mm, "end": v(-45.75, 64) * mm});
            skArc(sketch, "E140.19", {"start": v(-24.68, 20.3) * mm, "mid": v(-37.15, 23.88) * mm, "end": v(-43.24, 35.33) * mm});
            skLineSegment(sketch, "E140.20", {"start": v(30.45, 27.07) * mm, "end": v(-24.68, 20.3) * mm});
            skArc(sketch, "E140.21", {"start": v(42.8, 35.25) * mm, "mid": v(37.6, 29.7) * mm, "end": v(30.45, 27.07) * mm});
            skLineSegment(sketch, "E140.24", {"start": v(64.54, 43.3) * mm, "end": v(75.6, 62.46) * mm});
            skArc(sketch, "E140.25", {"start": v(65.94, 24.65) * mm, "mid": v(62.37, 33.76) * mm, "end": v(64.54, 43.3) * mm});
            skLineSegment(sketch, "E140.31", {"start": v(62.8, 69.86) * mm, "end": v(42.8, 35.25) * mm});
            skArc(sketch, "E140.32", {"start": v(-62.33, 24.81) * mm, "mid": v(-65.02, 22.35) * mm, "end": v(-68.2, 20.54) * mm});
            skLineSegment(sketch, "E140.33", {"start": v(-68.2, 20.54) * mm, "end": v(-81.35, 14.84) * mm});
            skArc(sketch, "E140.34", {"start": v(-81.35, 14.84) * mm, "mid": v(-82.84, 13.58) * mm, "end": v(-83.4, 11.72) * mm});
            skLineSegment(sketch, "E140.35", {"start": v(-83.4, 11.72) * mm, "end": v(-83.4, -11.72) * mm});
            skArc(sketch, "E140.36", {"start": v(-83.4, -11.72) * mm, "mid": v(-82.84, -13.58) * mm, "end": v(-81.35, -14.84) * mm});
            skLineSegment(sketch, "E140.37", {"start": v(-81.35, -14.84) * mm, "end": v(-68.2, -20.54) * mm});
            skArc(sketch, "E140.38", {"start": v(-68.2, -20.54) * mm, "mid": v(-65.02, -22.35) * mm, "end": v(-62.33, -24.81) * mm});
            skLineSegment(sketch, "E140.39", {"start": v(-58.26, -37.22) * mm, "end": v(-60.49, -62.7) * mm});
            skLineSegment(sketch, "E140.47", {"start": v(-45.75, -64) * mm, "end": v(-43.24, -35.33) * mm});
            skArc(sketch, "E140.48", {"start": v(-43.24, -35.33) * mm, "mid": v(-37.15, -23.88) * mm, "end": v(-24.68, -20.3) * mm});
            skLineSegment(sketch, "E140.49", {"start": v(-24.68, -20.3) * mm, "end": v(30.45, -27.07) * mm});
            skArc(sketch, "E140.50", {"start": v(30.45, -27.07) * mm, "mid": v(37.6, -29.7) * mm, "end": v(42.8, -35.25) * mm});
            skLineSegment(sketch, "E140.51", {"start": v(42.8, -35.25) * mm, "end": v(62.8, -69.86) * mm});
            skLineSegment(sketch, "E141", {"start": v(-60.49, -62.7) * mm, "end": v(-45.75, -64) * mm});
            skLineSegment(sketch, "E142", {"start": v(62.8, -69.86) * mm, "end": v(75.6, -62.46) * mm});
            skArc(sketch, "E143", {"start": v(-51.36, -29.74) * mm, "mid": v(-45.17, -23.02) * mm, "end": v(-54.3, -22.9) * mm});
            skArc(sketch, "E144", {"start": v(40.93, -27.18) * mm, "mid": v(47.1, -29.71) * mm, "end": v(50.3, -23.86) * mm});
            skLineSegment(sketch, "E145", {"start": v(64.38, -21.4) * mm, "end": v(52.25, -21.4) * mm});
            skArc(sketch, "E146.0", {"start": v(30.94, -23.1) * mm, "mid": v(36.2, -24.48) * mm, "end": v(40.93, -27.18) * mm});
            skLineSegment(sketch, "E146.1", {"start": v(8.86, -20.4) * mm, "end": v(30.94, -23.1) * mm});
            skPoint(sketch, "E147.visualSharp", {"position": v(48.9, -21.4) * mm});
            skArc(sketch, "E147.filletArc", {"start": v(52.25, -21.4) * mm, "mid": v(50.68, -22.16) * mm, "end": v(50.3, -23.86) * mm});
            skPoint(sketch, "E148.visualSharp", {"position": v(69.4, -21.4) * mm});
            skArc(sketch, "E148.filletArc", {"start": v(65.94, -24.65) * mm, "mid": v(66.18, -22.53) * mm, "end": v(64.38, -21.4) * mm});
            skPoint(sketch, "E149.visualSharp", {"position": v(-7.37, -18.4) * mm});
            skArc(sketch, "E149.filletArc", {"start": v(8.98, -18.4) * mm, "mid": v(7.98, -19.34) * mm, "end": v(8.86, -20.4) * mm});
            skFitSpline(sketch, "E150", {"points": [v(-62.55, -24.56) * mm, v(-57.79, -26.4) * mm, v(-54.3, -22.9) * mm], "startDerivative": vector(11.1, -12.78) * mm, "endDerivative": vector(6.86, 13.68) * mm});
            skFitSpline(sketch, "E151", {"points": [v(-58.26, -37.22) * mm, v(-56.74, -28.54) * mm, v(-51.36, -29.74) * mm], "startDerivative": vector(2.7, 21.07) * mm, "endDerivative": vector(15.18, -3.9) * mm});
            skLineSegment(sketch, "E152.MirrorCS", {"start": v(78.92, 18.4) * mm, "end": v(8.98, 18.4) * mm});
            skArc(sketch, "E153.MirrorCS", {"start": v(65.94, 24.65) * mm, "mid": v(66.18, 22.53) * mm, "end": v(64.38, 21.4) * mm});
            skLineSegment(sketch, "E154.MirrorCS", {"start": v(8.86, 20.4) * mm, "end": v(30.94, 23.1) * mm});
            skLineSegment(sketch, "E155.MirrorCS", {"start": v(64.38, 21.4) * mm, "end": v(52.25, 21.4) * mm});
            skArc(sketch, "E156.MirrorCS", {"start": v(52.25, 21.4) * mm, "mid": v(50.68, 22.16) * mm, "end": v(50.3, 23.86) * mm});
            skArc(sketch, "E157.MirrorCS", {"start": v(40.93, 27.18) * mm, "mid": v(47.1, 29.71) * mm, "end": v(50.3, 23.86) * mm});
            skArc(sketch, "E158.MirrorCS", {"start": v(30.94, 23.1) * mm, "mid": v(36.2, 24.48) * mm, "end": v(40.93, 27.18) * mm});
            skArc(sketch, "E159.MirrorCS", {"start": v(8.98, 18.4) * mm, "mid": v(7.98, 19.34) * mm, "end": v(8.86, 20.4) * mm});
            skArc(sketch, "E160.MirrorCS", {"start": v(-51.36, 29.74) * mm, "mid": v(-45.17, 23.02) * mm, "end": v(-54.3, 22.9) * mm});
            skFitSpline(sketch, "E161.MirrorCS", {"points": [v(-58.26, 37.22) * mm, v(-56.74, 28.54) * mm, v(-51.36, 29.74) * mm], "startDerivative": vector(2.7, -21.07) * mm, "endDerivative": vector(15.18, 3.9) * mm});
            skFitSpline(sketch, "E162.MirrorCS", {"points": [v(-62.55, 24.56) * mm, v(-57.79, 26.4) * mm, v(-54.3, 22.9) * mm], "startDerivative": vector(11.1, 12.78) * mm, "endDerivative": vector(6.86, -13.68) * mm});
            skLineSegment(sketch, "E163.MirrorCS", {"start": v(62.8, 69.86) * mm, "end": v(75.6, 62.46) * mm});
            skLineSegment(sketch, "E164.MirrorCS", {"start": v(-60.49, 62.7) * mm, "end": v(-45.75, 64) * mm});
            skSolve(sketch);
        }
        {
            var Q0;
            Q0=makeQuery(id+"F2.imprint","IMPRINT",FACE,{"disambiguationData":[TD([[makeQuery(id+"F2.imprint","IMPRINT",EDGE,{"derivedFrom":sQuery(id+"F2.wireOp",EDGE,"E133")}),-1.0]])]});
            extrude(context, id + "F3", {"entities" : qUnion([Q0]), "operationType" : NewBodyOperationType.REMOVE, "oppositeDirection" : true, "depth" : 7.4 * mm});
        }
        {
            var Q0;
            Q0=makeQuery(id+"F1.opExtrude","SWEPT_FACE",FACE,{"disambiguationData":[OSD([sQuery(id+"F0.wireOp",EDGE,"E12"),sQuery(id+"F0.wireOp",EDGE,"E108.MirrorCS")])]});
            var sketch = newSketch(context, id + "F4", { "sketchPlane" : qUnion([Q0])});
            skLineSegment(sketch, "E165.bottom", {"start": v(-13.5, 8) * mm, "end": v(-5.5, 8) * mm});
            skLineSegment(sketch, "E165.top", {"start": v(-13.5, 5) * mm, "end": v(-5.5, 5) * mm});
            skLineSegment(sketch, "E165.left", {"start": v(-13.5, 8) * mm, "end": v(-13.5, 5) * mm});
            skLineSegment(sketch, "E165.right", {"start": v(-5.5, 8) * mm, "end": v(-5.5, 5) * mm});
            skCircle(sketch, "E166", {"center": v(10, 1.1) * mm, "radius": 1 * mm});
            skSolve(sketch);
        }
        {
            var Q0;
            Q0=makeQuery(id+"F4.imprint","IMPRINT",FACE,{"disambiguationData":[TD([[makeQuery(id+"F4.imprint","IMPRINT",EDGE,{"derivedFrom":sQuery(id+"F4.wireOp",EDGE,"E165.bottom")}),-1.0]])]});
            var Q1;
            Q1=makeQuery(id+"F4.imprint","IMPRINT",FACE,{"disambiguationData":[TD([[makeQuery(id+"F4.imprint","IMPRINT",EDGE,{"derivedFrom":sQuery(id+"F4.wireOp",EDGE,"E166")}),1.0]])]});
            extrude(context, id + "F5", {"entities" : qUnion([Q0, Q1]), "operationType" : NewBodyOperationType.REMOVE, "oppositeDirection" : true, "depth" : 4 * mm});
        }
        {
            var Q0;
            Q0=makeQuery(id+"F3.boolean.opBoolean","COPY",FACE,{"derivedFrom":makeQuery(id+"F3.opExtrude","CAP_FACE",FACE,{"disambiguationData":[OSD([sQuery(id+"F0.wireOp",EDGE,"55a75c94-3981-4925-938c-0703a2540f2a"),sQuery(id+"F0.wireOp",EDGE,"18e9a88f-63d2-484e-94f8-6aafb132c643"),sQuery(id+"F0.wireOp",EDGE,"3e357946-6a65-48ba-9413-4c9084a4b4eb"),sQuery(id+"F0.wireOp",EDGE,"7aa77c07-5236-4930-a80c-88c67a00b59935.MirrorCS"),sQuery(id+"F0.wireOp",EDGE,"7aa77c07-5236-4930-a80c-88c67a00b59978.MirrorCS"),sQuery(id+"F0.wireOp",EDGE,"7aa77c07-5236-4930-a80c-88c67a00b59979.MirrorCS"),sQuery(id+"F0.wireOp",EDGE,"a4d90b42-d63e-410f-917a-941b09824992"),sQuery(id+"F2.wireOp",EDGE,"fffe1e67-2cc9-48c4-8983-8611bc80b19c.0"),sQuery(id+"F2.wireOp",EDGE,"fffe1e67-2cc9-48c4-8983-8611bc80b19c.1"),sQuery(id+"F2.wireOp",EDGE,"fffe1e67-2cc9-48c4-8983-8611bc80b19c.2"),sQuery(id+"F2.wireOp",EDGE,"2246689b-3c9b-4c8e-905d-07fedf87c73f.2"),sQuery(id+"F2.wireOp",EDGE,"d914186b-a5e1-4f1c-b080-cd34f5ce877f0.MirrorCS"),sQuery(id+"F2.wireOp",EDGE,"5fff3e55-b558-4c72-8411-46350b7e51440.MirrorCS"),sQuery(id+"F2.wireOp",EDGE,"5c2eff44-0bb9-47c2-831a-ff12a0e9dea30.MirrorCS"),sQuery(id+"F2.wireOp",EDGE,"a0e3ad08-1fbb-4ff4-acfc-af0f5074732f0.MirrorCS"),sQuery(id+"F2.wireOp",EDGE,"YLonHyPl-4aFv-fIO4-gWat-4KreMwAxru9C"),sQuery(id+"F2.wireOp",EDGE,"E133"),sQuery(id+"F2.wireOp",EDGE,"f0677aad-6ccf-4ac1-86a8-1c334f34c33b0.MirrorCS"),sQuery(id+"F2.wireOp",EDGE,"0db9f0e9-9e14-4ac0-91a2-759e6fbd4fb7.2.left"),sQuery(id+"F2.wireOp",EDGE,"abe0898a-1f7c-4316-9df3-18db7f33bf87"),sQuery(id+"F2.wireOp",EDGE,"20a845a6-1cc5-41a5-8aa5-076ad581321a"),sQuery(id+"F2.wireOp",EDGE,"50eb1c94-5ace-404b-bcef-2d3eae4a823a.filletArc"),sQuery(id+"F2.wireOp",EDGE,"05c023b2-4da7-4de4-8dc0-9080a339fc651.MirrorCS"),sQuery(id+"F2.wireOp",EDGE,"05c023b2-4da7-4de4-8dc0-9080a339fc657.MirrorCS"),sQuery(id+"F2.wireOp",EDGE,"05c023b2-4da7-4de4-8dc0-9080a339fc658.MirrorCS"),sQuery(id+"F2.wireOp",EDGE,"05c023b2-4da7-4de4-8dc0-9080a339fc659.MirrorCS"),sQuery(id+"F2.wireOp",EDGE,"0ITbmxvW-dEQf-i5GW-sRUa-ICrX6OYGrSRM"),sQuery(id+"F2.wireOp",EDGE,"81397a56-36e4-4d1a-aac4-778d4ba0b91e0.MirrorCS"),sQuery(id+"F2.wireOp",EDGE,"08d4352a-0a2f-4740-9c2c-cdb5e3f0d8b7.trimOffspring"),sQuery(id+"F2.wireOp",EDGE,"e74299a3-ef13-446a-a17a-9097ae4e11bd.trimOffspring"),sQuery(id+"F2.wireOp",EDGE,"ce151ea7-cdd1-498e-a54c-a8153daecff6.trimOffspring"),sQuery(id+"F2.wireOp",EDGE,"96f9a0b3-2fe5-4509-b9fd-21347e342cb5.trimOffspring"),sQuery(id+"F2.wireOp",EDGE,"E138.0.startCap"),sQuery(id+"F2.wireOp",EDGE,"E138.0.endCap"),sQuery(id+"F2.wireOp",EDGE,"E138.0.left"),sQuery(id+"F2.wireOp",EDGE,"E138.0.right"),sQuery(id+"F2.wireOp",EDGE,"E139.1.0.0"),sQuery(id+"F2.wireOp",EDGE,"E139.1.0.1"),sQuery(id+"F2.wireOp",EDGE,"E139.1.0.2"),sQuery(id+"F2.wireOp",EDGE,"E139.1.0.3"),sQuery(id+"F2.wireOp",EDGE,"E139.2.0.0"),sQuery(id+"F2.wireOp",EDGE,"E139.2.0.1"),sQuery(id+"F2.wireOp",EDGE,"E139.2.0.2"),sQuery(id+"F2.wireOp",EDGE,"E139.2.0.3")])],"isStart":false})});
            var sketch = newSketch(context, id + "F6", { "sketchPlane" : qUnion([Q0])});
            skLineSegment(sketch, "E167.bottom", {"start": v(49, 16) * mm, "end": v(81, 16) * mm});
            skLineSegment(sketch, "E167.top", {"start": v(49, -16) * mm, "end": v(81, -16) * mm});
            skLineSegment(sketch, "E167.left", {"start": v(49, 16) * mm, "end": v(49, -16) * mm});
            skLineSegment(sketch, "E167.right", {"start": v(81, 16) * mm, "end": v(81, -16) * mm});
            skSolve(sketch);
        }
        {
            var Q0;
            Q0=makeQuery(id+"F6.imprint","IMPRINT",FACE,{"disambiguationData":[TD([[makeQuery(id+"F6.imprint","IMPRINT",EDGE,{"derivedFrom":sQuery(id+"F6.wireOp",EDGE,"E167.bottom")}),-1.0]])]});
            extrude(context, id + "F7", {"entities" : qUnion([Q0]), "operationType" : NewBodyOperationType.REMOVE, "oppositeDirection" : true, "depth" : 1 * mm});
        }
        {
            var Q0;
            Q0=makeQuery(id+"F1.opExtrude","SWEPT_FACE",FACE,{"disambiguationData":[OSD([sQuery(id+"F0.wireOp",EDGE,"E116")])]});
            var sketch = newSketch(context, id + "F8", { "sketchPlane" : qUnion([Q0])});
            skCircle(sketch, "E168", {"center": v(-47.8, 8) * mm, "radius": 4 * mm});
            skSolve(sketch);
        }
        {
            var Q0;
            {var subQ0=sQuery(id+"F8.wireOp",EDGE,"E168");var subQ1=makeQuery(id+"F1.opExtrude","CAP_EDGE",EDGE,{"disambiguationData":[OSD([sQuery(id+"F0.wireOp",EDGE,"E116")])],"isStart":false});var subQ2=makeQuery(id+"F8.imprint","INTERSECT",VERTEX,{"disambiguationData":[OD(0.0)],"derivedFrom":[subQ1,subQ0]});Q0=makeQuery(id+"F8.imprint","IMPRINT",FACE,{"disambiguationData":[TD([[makeQuery(id+"F8.imprint","IMPRINT",EDGE,{"disambiguationData":[TD([[subQ2,1.0]])],"derivedFrom":subQ0}),1.0]])]});}
            extrude(context, id + "F9", {"entities" : qUnion([Q0]), "operationType" : NewBodyOperationType.REMOVE, "endBound" : BoundingType.UP_TO_NEXT, "oppositeDirection" : true, "depth" : 3 * mm});
        }
        {
            var Q0;
            Q0=makeQuery(id+"F1.opExtrude","SWEPT_FACE",FACE,{"disambiguationData":[OSD([sQuery(id+"F0.wireOp",EDGE,"E118")])]});
            var sketch = newSketch(context, id + "F10", { "sketchPlane" : qUnion([Q0])});
            skCircle(sketch, "E169", {"center": v(26.45, 8) * mm, "radius": 4 * mm});
            skSolve(sketch);
        }
        {
            var Q0;
            Q0=makeQuery(id+"F1.opExtrude","SWEPT_FACE",FACE,{"disambiguationData":[OSD([sQuery(id+"F0.wireOp",EDGE,"E6")])]});
            cPlane(context, id + "F11", {"entities" : qUnion([Q0]), "cplaneType" : CPlaneType.OFFSET, "offset" : 9 * mm, "oppositeDirection" : true, "width" : 150 * mm, "height" : 150 * mm});
        }
        {
            var Q0;
            Q0=qCreatedBy(id+"F11.planeOp",FACE);
            var sketch = newSketch(context, id + "F12", { "sketchPlane" : qUnion([Q0])});
            skLineSegment(sketch, "E170.bottom", {"start": v(94.34, 2) * mm, "end": v(84.34, 2) * mm});
            skLineSegment(sketch, "E170.top", {"start": v(94.34, 6) * mm, "end": v(84.34, 6) * mm});
            skLineSegment(sketch, "E170.left", {"start": v(94.34, 2) * mm, "end": v(94.34, 6) * mm});
            skLineSegment(sketch, "E170.right", {"start": v(84.34, 2) * mm, "end": v(84.34, 6) * mm});
            skPoint(sketch, "E170.middle", {"position": v(89.34, 4) * mm});
            skSolve(sketch);
        }
        {
            var Q0;
            Q0=qSketchRegion(id+"F12",true);
            extrude(context, id + "F13", {"entities" : qUnion([Q0]), "operationType" : NewBodyOperationType.REMOVE, "endBound" : BoundingType.SYMMETRIC, "oppositeDirection" : true, "depth" : 40 * mm});
        }
        {
            var Q0;
            Q0=makeQuery(id+"F1.opExtrude","SWEPT_FACE",FACE,{"disambiguationData":[OSD([sQuery(id+"F0.wireOp",EDGE,"E95.MirrorCS")])]});
            cPlane(context, id + "F14", {"entities" : qUnion([Q0]), "cplaneType" : CPlaneType.OFFSET, "offset" : 9 * mm, "oppositeDirection" : true, "width" : 150 * mm, "height" : 150 * mm});
        }
        {
            var Q0;
            Q0=qCreatedBy(id+"F14.planeOp",FACE);
            var sketch = newSketch(context, id + "F15", { "sketchPlane" : qUnion([Q0])});
            skLineSegment(sketch, "E171.bottom", {"start": v(118.5, 2) * mm, "end": v(108.5, 2) * mm});
            skLineSegment(sketch, "E171.top", {"start": v(118.5, 6) * mm, "end": v(108.5, 6) * mm});
            skLineSegment(sketch, "E171.left", {"start": v(118.5, 2) * mm, "end": v(118.5, 6) * mm});
            skLineSegment(sketch, "E171.right", {"start": v(108.5, 2) * mm, "end": v(108.5, 6) * mm});
            skPoint(sketch, "E171.middle", {"position": v(113.5, 4) * mm});
            skSolve(sketch);
        }
        {
            var Q0;
            Q0=makeQuery(id+"F15.imprint","IMPRINT",FACE,{"disambiguationData":[TD([[makeQuery(id+"F15.imprint","IMPRINT",EDGE,{"derivedFrom":sQuery(id+"F15.wireOp",EDGE,"E171.bottom")}),-1.0]])]});
            extrude(context, id + "F16", {"entities" : qUnion([Q0]), "operationType" : NewBodyOperationType.REMOVE, "endBound" : BoundingType.SYMMETRIC, "oppositeDirection" : true, "depth" : 40 * mm});
        }
        {
            var Q0;
            {var subQ0=sQuery(id+"F15.wireOp",EDGE,"E171.bottom");var subQ1=sQuery(id+"F15.wireOp",EDGE,"E171.right");Q0=makeQuery(id+"F16.boolean.opBoolean","COPY",EDGE,{"disambiguationData":[TD([makeQuery(id+"F1.opExtrude","SWEPT_FACE",FACE,{"disambiguationData":[OSD([sQuery(id+"F0.wireOp",EDGE,"E89.MirrorCS")])]})])],"derivedFrom":makeQuery(id+"F16.opExtrude","SWEPT_EDGE",EDGE,{"disambiguationData":[OSD([subQ0,subQ1])]})});}
            var Q1;
            {var subQ0=sQuery(id+"F15.wireOp",EDGE,"E171.top");var subQ1=sQuery(id+"F15.wireOp",EDGE,"E171.right");Q1=makeQuery(id+"F16.boolean.opBoolean","COPY",EDGE,{"disambiguationData":[TD([makeQuery(id+"F1.opExtrude","SWEPT_FACE",FACE,{"disambiguationData":[OSD([sQuery(id+"F0.wireOp",EDGE,"E89.MirrorCS")])]})])],"derivedFrom":makeQuery(id+"F16.opExtrude","SWEPT_EDGE",EDGE,{"disambiguationData":[OSD([subQ0,subQ1])]})});}
            var Q2;
            {var subQ0=sQuery(id+"F15.wireOp",EDGE,"E171.top");var subQ1=sQuery(id+"F15.wireOp",EDGE,"E171.left");Q2=makeQuery(id+"F16.boolean.opBoolean","COPY",EDGE,{"disambiguationData":[TD([makeQuery(id+"F1.opExtrude","SWEPT_FACE",FACE,{"disambiguationData":[OSD([sQuery(id+"F0.wireOp",EDGE,"E89.MirrorCS")])]})])],"derivedFrom":makeQuery(id+"F16.opExtrude","SWEPT_EDGE",EDGE,{"disambiguationData":[OSD([subQ0,subQ1])]})});}
            var Q3;
            {var subQ0=sQuery(id+"F15.wireOp",EDGE,"E171.bottom");var subQ1=sQuery(id+"F15.wireOp",EDGE,"E171.left");Q3=makeQuery(id+"F16.boolean.opBoolean","COPY",EDGE,{"disambiguationData":[TD([makeQuery(id+"F1.opExtrude","SWEPT_FACE",FACE,{"disambiguationData":[OSD([sQuery(id+"F0.wireOp",EDGE,"E89.MirrorCS")])]})])],"derivedFrom":makeQuery(id+"F16.opExtrude","SWEPT_EDGE",EDGE,{"disambiguationData":[OSD([subQ0,subQ1])]})});}
            var Q4;
            {var subQ0=sQuery(id+"F15.wireOp",EDGE,"E171.left");var subQ1=sQuery(id+"F15.wireOp",EDGE,"E171.bottom");Q4=makeQuery(id+"F16.boolean.opBoolean","COPY",EDGE,{"disambiguationData":[TD([makeQuery(id+"F1.opExtrude","SWEPT_FACE",FACE,{"disambiguationData":[OSD([sQuery(id+"F0.wireOp",EDGE,"E86.MirrorCS")])]})])],"derivedFrom":makeQuery(id+"F16.opExtrude","SWEPT_EDGE",EDGE,{"disambiguationData":[OSD([subQ1,subQ0])]})});}
            var Q5;
            {var subQ0=sQuery(id+"F15.wireOp",EDGE,"E171.bottom");var subQ1=sQuery(id+"F15.wireOp",EDGE,"E171.right");Q5=makeQuery(id+"F16.boolean.opBoolean","COPY",EDGE,{"disambiguationData":[TD([makeQuery(id+"F1.opExtrude","SWEPT_FACE",FACE,{"disambiguationData":[OSD([sQuery(id+"F0.wireOp",EDGE,"E86.MirrorCS")])]})])],"derivedFrom":makeQuery(id+"F16.opExtrude","SWEPT_EDGE",EDGE,{"disambiguationData":[OSD([subQ0,subQ1])]})});}
            var Q6;
            {var subQ0=sQuery(id+"F15.wireOp",EDGE,"E171.top");var subQ1=sQuery(id+"F15.wireOp",EDGE,"E171.right");Q6=makeQuery(id+"F16.boolean.opBoolean","COPY",EDGE,{"disambiguationData":[TD([makeQuery(id+"F1.opExtrude","SWEPT_FACE",FACE,{"disambiguationData":[OSD([sQuery(id+"F0.wireOp",EDGE,"E86.MirrorCS")])]})])],"derivedFrom":makeQuery(id+"F16.opExtrude","SWEPT_EDGE",EDGE,{"disambiguationData":[OSD([subQ0,subQ1])]})});}
            var Q7;
            {var subQ0=sQuery(id+"F15.wireOp",EDGE,"E171.top");var subQ1=sQuery(id+"F15.wireOp",EDGE,"E171.left");Q7=makeQuery(id+"F16.boolean.opBoolean","COPY",EDGE,{"disambiguationData":[TD([makeQuery(id+"F1.opExtrude","SWEPT_FACE",FACE,{"disambiguationData":[OSD([sQuery(id+"F0.wireOp",EDGE,"E86.MirrorCS")])]})])],"derivedFrom":makeQuery(id+"F16.opExtrude","SWEPT_EDGE",EDGE,{"disambiguationData":[OSD([subQ0,subQ1])]})});}
            var Q8;
            {var subQ0=sQuery(id+"F12.wireOp",EDGE,"E170.right");var subQ1=sQuery(id+"F12.wireOp",EDGE,"E170.top");Q8=makeQuery(id+"FrttgUIXkOwAJPR_1.1.F13.boolean.opBoolean","COPY",EDGE,{"disambiguationData":[TD([makeQuery(id+"F1.opExtrude","SWEPT_FACE",FACE,{"disambiguationData":[OSD([sQuery(id+"F0.wireOp",EDGE,"E79.MirrorCS")])]})])],"derivedFrom":makeQuery(id+"FrttgUIXkOwAJPR_1.1.F13.opExtrude","SWEPT_EDGE",EDGE,{"disambiguationData":[OSD([subQ1,subQ0])]})});}
            var Q9;
            {var subQ0=sQuery(id+"F12.wireOp",EDGE,"E170.bottom");var subQ1=sQuery(id+"F12.wireOp",EDGE,"E170.right");Q9=makeQuery(id+"FrttgUIXkOwAJPR_1.1.F13.boolean.opBoolean","COPY",EDGE,{"disambiguationData":[TD([makeQuery(id+"F1.opExtrude","SWEPT_FACE",FACE,{"disambiguationData":[OSD([sQuery(id+"F0.wireOp",EDGE,"E79.MirrorCS")])]})])],"derivedFrom":makeQuery(id+"FrttgUIXkOwAJPR_1.1.F13.opExtrude","SWEPT_EDGE",EDGE,{"disambiguationData":[OSD([subQ0,subQ1])]})});}
            var Q10;
            {var subQ0=sQuery(id+"F12.wireOp",EDGE,"E170.bottom");var subQ1=sQuery(id+"F12.wireOp",EDGE,"E170.right");Q10=makeQuery(id+"FrttgUIXkOwAJPR_1.1.F13.boolean.opBoolean","COPY",EDGE,{"disambiguationData":[TD([makeQuery(id+"F1.opExtrude","SWEPT_FACE",FACE,{"disambiguationData":[OSD([sQuery(id+"F0.wireOp",EDGE,"E87.MirrorCS")])]})])],"derivedFrom":makeQuery(id+"FrttgUIXkOwAJPR_1.1.F13.opExtrude","SWEPT_EDGE",EDGE,{"disambiguationData":[OSD([subQ0,subQ1])]})});}
            var Q11;
            {var subQ0=sQuery(id+"F12.wireOp",EDGE,"E170.bottom");var subQ1=sQuery(id+"F12.wireOp",EDGE,"E170.left");Q11=makeQuery(id+"FrttgUIXkOwAJPR_1.1.F13.boolean.opBoolean","COPY",EDGE,{"disambiguationData":[TD([makeQuery(id+"F1.opExtrude","SWEPT_FACE",FACE,{"disambiguationData":[OSD([sQuery(id+"F0.wireOp",EDGE,"E79.MirrorCS")])]})])],"derivedFrom":makeQuery(id+"FrttgUIXkOwAJPR_1.1.F13.opExtrude","SWEPT_EDGE",EDGE,{"disambiguationData":[OSD([subQ0,subQ1])]})});}
            var Q12;
            {var subQ0=sQuery(id+"F12.wireOp",EDGE,"E170.top");var subQ1=sQuery(id+"F12.wireOp",EDGE,"E170.left");Q12=makeQuery(id+"FrttgUIXkOwAJPR_1.1.F13.boolean.opBoolean","COPY",EDGE,{"disambiguationData":[TD([makeQuery(id+"F1.opExtrude","SWEPT_FACE",FACE,{"disambiguationData":[OSD([sQuery(id+"F0.wireOp",EDGE,"E79.MirrorCS")])]})])],"derivedFrom":makeQuery(id+"FrttgUIXkOwAJPR_1.1.F13.opExtrude","SWEPT_EDGE",EDGE,{"disambiguationData":[OSD([subQ0,subQ1])]})});}
            var Q13;
            {var subQ0=sQuery(id+"F12.wireOp",EDGE,"E170.top");var subQ1=sQuery(id+"F12.wireOp",EDGE,"E170.left");Q13=makeQuery(id+"FrttgUIXkOwAJPR_1.1.F13.boolean.opBoolean","COPY",EDGE,{"disambiguationData":[TD([makeQuery(id+"F1.opExtrude","SWEPT_FACE",FACE,{"disambiguationData":[OSD([sQuery(id+"F0.wireOp",EDGE,"E87.MirrorCS")])]})])],"derivedFrom":makeQuery(id+"FrttgUIXkOwAJPR_1.1.F13.opExtrude","SWEPT_EDGE",EDGE,{"disambiguationData":[OSD([subQ0,subQ1])]})});}
            var Q14;
            {var subQ0=sQuery(id+"F12.wireOp",EDGE,"E170.bottom");var subQ1=sQuery(id+"F12.wireOp",EDGE,"E170.left");Q14=makeQuery(id+"FrttgUIXkOwAJPR_1.1.F13.boolean.opBoolean","COPY",EDGE,{"disambiguationData":[TD([makeQuery(id+"F1.opExtrude","SWEPT_FACE",FACE,{"disambiguationData":[OSD([sQuery(id+"F0.wireOp",EDGE,"E87.MirrorCS")])]})])],"derivedFrom":makeQuery(id+"FrttgUIXkOwAJPR_1.1.F13.opExtrude","SWEPT_EDGE",EDGE,{"disambiguationData":[OSD([subQ0,subQ1])]})});}
            var Q15;
            {var subQ0=sQuery(id+"F12.wireOp",EDGE,"E170.right");var subQ1=sQuery(id+"F12.wireOp",EDGE,"E170.top");Q15=makeQuery(id+"FrttgUIXkOwAJPR_1.1.F13.boolean.opBoolean","COPY",EDGE,{"disambiguationData":[TD([makeQuery(id+"F1.opExtrude","SWEPT_FACE",FACE,{"disambiguationData":[OSD([sQuery(id+"F0.wireOp",EDGE,"E87.MirrorCS")])]})])],"derivedFrom":makeQuery(id+"FrttgUIXkOwAJPR_1.1.F13.opExtrude","SWEPT_EDGE",EDGE,{"disambiguationData":[OSD([subQ1,subQ0])]})});}
            var Q16;
            {var subQ0=sQuery(id+"F15.wireOp",EDGE,"E171.bottom");var subQ1=sQuery(id+"F15.wireOp",EDGE,"E171.right");Q16=makeQuery(id+"FyABKiLMpsOIMja_1.1.F16.boolean.opBoolean","COPY",EDGE,{"disambiguationData":[TD([makeQuery(id+"F1.opExtrude","SWEPT_FACE",FACE,{"disambiguationData":[OSD([sQuery(id+"F0.wireOp",EDGE,"E32.trimOffspring")])]})])],"derivedFrom":makeQuery(id+"FyABKiLMpsOIMja_1.1.F16.opExtrude","SWEPT_EDGE",EDGE,{"disambiguationData":[OSD([subQ0,subQ1])]})});}
            var Q17;
            {var subQ0=sQuery(id+"F15.wireOp",EDGE,"E171.bottom");var subQ1=sQuery(id+"F15.wireOp",EDGE,"E171.right");Q17=makeQuery(id+"FyABKiLMpsOIMja_1.1.F16.boolean.opBoolean","COPY",EDGE,{"disambiguationData":[TD([makeQuery(id+"F1.opExtrude","SWEPT_FACE",FACE,{"disambiguationData":[OSD([sQuery(id+"F0.wireOp",EDGE,"E4")])]})])],"derivedFrom":makeQuery(id+"FyABKiLMpsOIMja_1.1.F16.opExtrude","SWEPT_EDGE",EDGE,{"disambiguationData":[OSD([subQ0,subQ1])]})});}
            var Q18;
            {var subQ0=sQuery(id+"F15.wireOp",EDGE,"E171.bottom");var subQ1=sQuery(id+"F15.wireOp",EDGE,"E171.left");Q18=makeQuery(id+"FyABKiLMpsOIMja_1.1.F16.boolean.opBoolean","COPY",EDGE,{"disambiguationData":[TD([makeQuery(id+"F1.opExtrude","SWEPT_FACE",FACE,{"disambiguationData":[OSD([sQuery(id+"F0.wireOp",EDGE,"E32.trimOffspring")])]})])],"derivedFrom":makeQuery(id+"FyABKiLMpsOIMja_1.1.F16.opExtrude","SWEPT_EDGE",EDGE,{"disambiguationData":[OSD([subQ0,subQ1])]})});}
            var Q19;
            {var subQ0=sQuery(id+"F15.wireOp",EDGE,"E171.top");var subQ1=sQuery(id+"F15.wireOp",EDGE,"E171.left");Q19=makeQuery(id+"FyABKiLMpsOIMja_1.1.F16.boolean.opBoolean","COPY",EDGE,{"disambiguationData":[TD([makeQuery(id+"F1.opExtrude","SWEPT_FACE",FACE,{"disambiguationData":[OSD([sQuery(id+"F0.wireOp",EDGE,"E32.trimOffspring")])]})])],"derivedFrom":makeQuery(id+"FyABKiLMpsOIMja_1.1.F16.opExtrude","SWEPT_EDGE",EDGE,{"disambiguationData":[OSD([subQ0,subQ1])]})});}
            var Q20;
            {var subQ0=sQuery(id+"F15.wireOp",EDGE,"E171.top");var subQ1=sQuery(id+"F15.wireOp",EDGE,"E171.right");Q20=makeQuery(id+"FyABKiLMpsOIMja_1.1.F16.boolean.opBoolean","COPY",EDGE,{"disambiguationData":[TD([makeQuery(id+"F1.opExtrude","SWEPT_FACE",FACE,{"disambiguationData":[OSD([sQuery(id+"F0.wireOp",EDGE,"E32.trimOffspring")])]})])],"derivedFrom":makeQuery(id+"FyABKiLMpsOIMja_1.1.F16.opExtrude","SWEPT_EDGE",EDGE,{"disambiguationData":[OSD([subQ0,subQ1])]})});}
            var Q21;
            {var subQ0=sQuery(id+"F12.wireOp",EDGE,"E170.top");var subQ1=sQuery(id+"F12.wireOp",EDGE,"E170.left");Q21=makeQuery(id+"F13.boolean.opBoolean","COPY",EDGE,{"disambiguationData":[TD([makeQuery(id+"F1.opExtrude","SWEPT_FACE",FACE,{"disambiguationData":[OSD([sQuery(id+"F0.wireOp",EDGE,"E29.trimOffspring")])]})])],"derivedFrom":makeQuery(id+"F13.opExtrude","SWEPT_EDGE",EDGE,{"disambiguationData":[OSD([subQ0,subQ1])]})});}
            var Q22;
            {var subQ0=sQuery(id+"F12.wireOp",EDGE,"E170.top");var subQ1=sQuery(id+"F12.wireOp",EDGE,"E170.left");Q22=makeQuery(id+"F13.boolean.opBoolean","COPY",EDGE,{"disambiguationData":[TD([makeQuery(id+"F1.opExtrude","SWEPT_FACE",FACE,{"disambiguationData":[OSD([sQuery(id+"F0.wireOp",EDGE,"E3")])]})])],"derivedFrom":makeQuery(id+"F13.opExtrude","SWEPT_EDGE",EDGE,{"disambiguationData":[OSD([subQ0,subQ1])]})});}
            var Q23;
            {var subQ0=sQuery(id+"F12.wireOp",EDGE,"E170.right");var subQ1=sQuery(id+"F12.wireOp",EDGE,"E170.top");Q23=makeQuery(id+"F13.boolean.opBoolean","COPY",EDGE,{"disambiguationData":[TD([makeQuery(id+"F1.opExtrude","SWEPT_FACE",FACE,{"disambiguationData":[OSD([sQuery(id+"F0.wireOp",EDGE,"E3")])]})])],"derivedFrom":makeQuery(id+"F13.opExtrude","SWEPT_EDGE",EDGE,{"disambiguationData":[OSD([subQ1,subQ0])]})});}
            var Q24;
            {var subQ0=sQuery(id+"F12.wireOp",EDGE,"E170.top");var subQ1=sQuery(id+"F12.wireOp",EDGE,"E170.right");Q24=makeQuery(id+"F13.boolean.opBoolean","COPY",EDGE,{"disambiguationData":[TD([makeQuery(id+"F1.opExtrude","SWEPT_FACE",FACE,{"disambiguationData":[OSD([sQuery(id+"F0.wireOp",EDGE,"E29.trimOffspring")])]})])],"derivedFrom":makeQuery(id+"F13.opExtrude","SWEPT_EDGE",EDGE,{"disambiguationData":[OSD([subQ0,subQ1])]})});}
            var Q25;
            {var subQ0=sQuery(id+"F12.wireOp",EDGE,"E170.bottom");var subQ1=sQuery(id+"F12.wireOp",EDGE,"E170.right");Q25=makeQuery(id+"F13.boolean.opBoolean","COPY",EDGE,{"disambiguationData":[TD([makeQuery(id+"F1.opExtrude","SWEPT_FACE",FACE,{"disambiguationData":[OSD([sQuery(id+"F0.wireOp",EDGE,"E3")])]})])],"derivedFrom":makeQuery(id+"F13.opExtrude","SWEPT_EDGE",EDGE,{"disambiguationData":[OSD([subQ0,subQ1])]})});}
            var Q26;
            {var subQ0=sQuery(id+"F12.wireOp",EDGE,"E170.bottom");var subQ1=sQuery(id+"F12.wireOp",EDGE,"E170.right");Q26=makeQuery(id+"F13.boolean.opBoolean","COPY",EDGE,{"disambiguationData":[TD([makeQuery(id+"F1.opExtrude","SWEPT_FACE",FACE,{"disambiguationData":[OSD([sQuery(id+"F0.wireOp",EDGE,"E29.trimOffspring")])]})])],"derivedFrom":makeQuery(id+"F13.opExtrude","SWEPT_EDGE",EDGE,{"disambiguationData":[OSD([subQ0,subQ1])]})});}
            var Q27;
            {var subQ0=sQuery(id+"F12.wireOp",EDGE,"E170.bottom");var subQ1=sQuery(id+"F12.wireOp",EDGE,"E170.left");Q27=makeQuery(id+"F13.boolean.opBoolean","COPY",EDGE,{"disambiguationData":[TD([makeQuery(id+"F1.opExtrude","SWEPT_FACE",FACE,{"disambiguationData":[OSD([sQuery(id+"F0.wireOp",EDGE,"E29.trimOffspring")])]})])],"derivedFrom":makeQuery(id+"F13.opExtrude","SWEPT_EDGE",EDGE,{"disambiguationData":[OSD([subQ0,subQ1])]})});}
            var Q28;
            {var subQ0=sQuery(id+"F12.wireOp",EDGE,"E170.bottom");var subQ1=sQuery(id+"F12.wireOp",EDGE,"E170.left");Q28=makeQuery(id+"F13.boolean.opBoolean","COPY",EDGE,{"disambiguationData":[TD([makeQuery(id+"F1.opExtrude","SWEPT_FACE",FACE,{"disambiguationData":[OSD([sQuery(id+"F0.wireOp",EDGE,"E3")])]})])],"derivedFrom":makeQuery(id+"F13.opExtrude","SWEPT_EDGE",EDGE,{"disambiguationData":[OSD([subQ0,subQ1])]})});}
            var Q29;
            {var subQ0=sQuery(id+"F15.wireOp",EDGE,"E171.left");var subQ1=sQuery(id+"F15.wireOp",EDGE,"E171.top");Q29=makeQuery(id+"FyABKiLMpsOIMja_1.1.F16.boolean.opBoolean","COPY",EDGE,{"disambiguationData":[TD([makeQuery(id+"F1.opExtrude","SWEPT_FACE",FACE,{"disambiguationData":[OSD([sQuery(id+"F0.wireOp",EDGE,"E4")])]})])],"derivedFrom":makeQuery(id+"FyABKiLMpsOIMja_1.1.F16.opExtrude","SWEPT_EDGE",EDGE,{"disambiguationData":[OSD([subQ1,subQ0])]})});}
            var Q30;
            {var subQ0=sQuery(id+"F15.wireOp",EDGE,"E171.top");var subQ1=sQuery(id+"F15.wireOp",EDGE,"E171.right");Q30=makeQuery(id+"FyABKiLMpsOIMja_1.1.F16.boolean.opBoolean","COPY",EDGE,{"disambiguationData":[TD([makeQuery(id+"F1.opExtrude","SWEPT_FACE",FACE,{"disambiguationData":[OSD([sQuery(id+"F0.wireOp",EDGE,"E4")])]})])],"derivedFrom":makeQuery(id+"FyABKiLMpsOIMja_1.1.F16.opExtrude","SWEPT_EDGE",EDGE,{"disambiguationData":[OSD([subQ0,subQ1])]})});}
            var Q31;
            {var subQ0=sQuery(id+"F15.wireOp",EDGE,"E171.left");var subQ1=sQuery(id+"F15.wireOp",EDGE,"E171.bottom");Q31=makeQuery(id+"FyABKiLMpsOIMja_1.1.F16.boolean.opBoolean","COPY",EDGE,{"disambiguationData":[TD([makeQuery(id+"F1.opExtrude","SWEPT_FACE",FACE,{"disambiguationData":[OSD([sQuery(id+"F0.wireOp",EDGE,"E4")])]})])],"derivedFrom":makeQuery(id+"FyABKiLMpsOIMja_1.1.F16.opExtrude","SWEPT_EDGE",EDGE,{"disambiguationData":[OSD([subQ1,subQ0])]})});}
            fillet(context, id + "F17", {"entities" : qUnion([Q0, Q1, Q2, Q3, Q4, Q5, Q6, Q7, Q8, Q9, Q10, Q11, Q12, Q13, Q14, Q15, Q16, Q17, Q18, Q19, Q20, Q21, Q22, Q23, Q24, Q25, Q26, Q27, Q28, Q29, Q30, Q31]), "radius" : 2 * mm, "tangentPropagation" : true, "allowEdgeOverflow" : false});
        }
        {
            var Q0;
            {var subQ0=sQuery(id+"F10.wireOp",EDGE,"E169");var subQ1=makeQuery(id+"F1.opExtrude","CAP_EDGE",EDGE,{"disambiguationData":[OSD([sQuery(id+"F0.wireOp",EDGE,"E118")])],"isStart":false});var subQ2=makeQuery(id+"F10.imprint","INTERSECT",VERTEX,{"disambiguationData":[OD(0.0)],"derivedFrom":[subQ1,subQ0]});Q0=makeQuery(id+"F10.imprint","IMPRINT",FACE,{"disambiguationData":[TD([[makeQuery(id+"F10.imprint","IMPRINT",EDGE,{"disambiguationData":[TD([[subQ2,1.0]])],"derivedFrom":subQ0}),1.0]])]});}
            extrude(context, id + "F18", {"entities" : qUnion([Q0]), "operationType" : NewBodyOperationType.REMOVE, "endBound" : BoundingType.UP_TO_NEXT, "oppositeDirection" : true, "depth" : 25 * mm});
        }
    });
